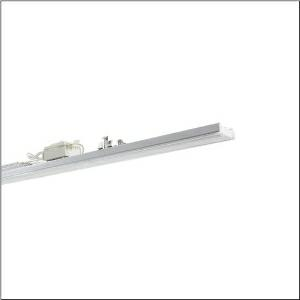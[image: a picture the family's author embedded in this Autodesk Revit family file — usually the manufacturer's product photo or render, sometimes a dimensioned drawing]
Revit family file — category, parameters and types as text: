
# Revit family: licross_r__11_recessed_ho_51tl1wmn4exm_7c4f
name_source: partatom
category: Lighting Fixtures
units: mm (PartAtom-declared; Revit-internal decimal feet)

## family parameters
Cut with Voids When Loaded = No
Host = Face
Light Source = No
Part Type = Normal
Room Calculation Point = No
Round Connector Dimension = Use Diameter
Shared = No

## types (1)
- --- (1 x LED, 14240 lm, 74.5 W, 4000K)
    Apparent Load = 75 VA
    CIE Flux Codes = 73 94 99 100 100
    Color Rendering = 80
    Color Temperature = 4000K
    Default Elevation = 1800 mm
    Description = Licross® 11 Recessed HO, luminaire insert, of sheet steel, coil coated, white, length: 1.500mm, width: 66mm, height: 67mm, LED rated luminous flux: 14.240lm, light colour: 840, control gear: ON/OFF Multilumen, with plug, 3-pole, with phase selection, mains connection: 220..240V, AC, 50/60Hz, rated input power: 75W, internal wiring halogen-free, primary optical cover: cover, of PMMA, light emission: direct distribution, primary light characteristic: symmetric, protection rating (complete): IP40, insulation class (complete): insulation class I (protective earthing), certification: CE, ENEC, VDE, UKCA, protection symbol: D if used in an environment without relevant dust loads with corresponding accessories, impact resistance: IK06, permissible ambient temperature for indoor applications: -35..+35°C, corresponds to IFS (International Featured Standards) requirements for safety and quality in the food industry, reducing of maximum allowable ambient temperature of 5°C with ceiling mounting, packaging unit: 1 piece
    Height = 58 mm
    Lamp = 1 x LED
    Lamp Light Flux = 14240 lm
    Lamp Power = 74.5 W
    Lamp count = 1
    Length = 1500 mm
    Luminous efficacy = 191 lm/W
    Manufacturer = Siteco
    ModVariant = No
    Model = 51TL1WMN4EXM
    Mounting Place = Ceiling
    Mounting Type = Pendant
    Number of Poles = 1
    OnlyDefault = Yes
    Power Factor = 1
    Product Name = Licross® 11 Recessed HO
    Product group = luminaire insert | ceiling pendant
    ProductGroupID = 902
    Protection Class = Protection class I
    Protection Degree = IP 40
    RLX_Detail_Level = 1
    RLX_Emergency_Light_Flux = 0 lm
    RLX_Emergency_Type = 0
    RLX_Emergency_Type_DB = No
    RlxData = <blob elided: 22197 chars, md5=9792eff5>
    Socket = socket
    Standby Power = 0 W
    System Light Flux = 14240 lm
    System Power = 75 W
    Type Comments = factory setting: luminous flux: 100 % | (A | C | E) | 174 mA
    Type Image = l_1296930.jpg
    URL = http://relux.com
    VarID = @adj_079377
    Voltage = 0 V
    Weight = 0.00 kg
    Width = 66 mm

## geometry (parser evidence)
native form markers: Blend x4, Sweep x11
no freeform markers — native parametric forms only
